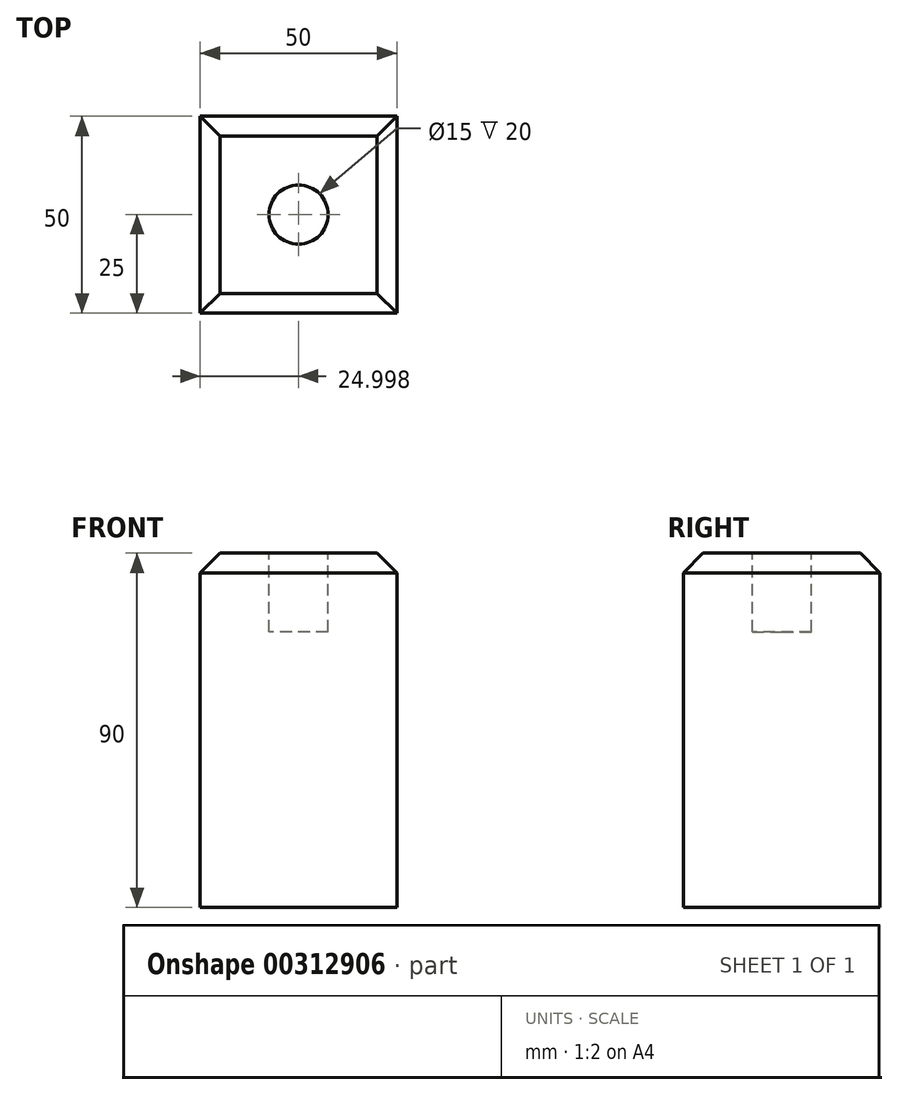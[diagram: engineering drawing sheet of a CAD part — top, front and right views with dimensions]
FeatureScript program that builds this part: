
annotation { "Feature Type Name" : "Feature", "Feature Type Description" : "" }
export const myFeature = defineFeature(function(context is Context, id is Id, definition is map)
    precondition{}
    {
        {
            var Q0;
            Q0=qCreatedBy(makeId("Top.planeOp"),FACE);
            var sketch = newSketch(context, id + "F0", { "sketchPlane" : qUnion([Q0])});
            skLineSegment(sketch, "E0", {"start": v(-33.76, -27.68) * mm, "end": v(-33.76, 22.32) * mm});
            skLineSegment(sketch, "E1", {"start": v(-33.76, 22.32) * mm, "end": v(16.24, 22.32) * mm});
            skLineSegment(sketch, "E2", {"start": v(16.24, 22.32) * mm, "end": v(16.24, -27.68) * mm});
            skLineSegment(sketch, "E3", {"start": v(16.24, -27.68) * mm, "end": v(-33.76, -27.68) * mm});
            skSolve(sketch);
        }
        {
            var Q0;
            Q0=makeQuery(id+"F0.imprint","IMPRINT",FACE,{"disambiguationData":[TD([[makeQuery(id+"F0.imprint","IMPRINT",EDGE,{"derivedFrom":sQuery(id+"F0.wireOp",EDGE,"E0")}),-1.0]])]});
            extrude(context, id + "F1", {"entities" : qUnion([Q0]), "depth" : 90 * mm});
        }
        {
            var Q0;
            Q0=makeQuery(id+"F1.opExtrude","CAP_FACE",FACE,{"disambiguationData":[OSD([sQuery(id+"F0.wireOp",EDGE,"E0"),sQuery(id+"F0.wireOp",EDGE,"E1"),sQuery(id+"F0.wireOp",EDGE,"E2"),sQuery(id+"F0.wireOp",EDGE,"E3")])],"isStart":false});
            chamfer(context, id + "F2", {"entities" : qUnion([Q0]), "width" : 5 * mm, "tangentPropagation" : true});
        }
        {
            var Q0;
            Q0=makeQuery(id+"F1.opExtrude","CAP_FACE",FACE,{"disambiguationData":[OSD([sQuery(id+"F0.wireOp",EDGE,"E0"),sQuery(id+"F0.wireOp",EDGE,"E1"),sQuery(id+"F0.wireOp",EDGE,"E2"),sQuery(id+"F0.wireOp",EDGE,"E3")])],"isStart":false});
            var sketch = newSketch(context, id + "F3", { "sketchPlane" : qUnion([Q0])});
            skSolve(sketch);
        }
        {
            var Q0;
            {var subQ0=sQuery(id+"F0.wireOp",EDGE,"E3");var subQ1=sQuery(id+"F0.wireOp",EDGE,"E2");var subQ2=sQuery(id+"F0.wireOp",EDGE,"E1");var subQ3=sQuery(id+"F0.wireOp",EDGE,"E0");var subQ4=makeQuery(id+"F1.opExtrude","CAP_FACE",FACE,{"disambiguationData":[OSD([subQ3,subQ2,subQ1,subQ0])],"isStart":false});Q0=makeQuery(id+"F3.imprint","IMPRINT",FACE,{"disambiguationData":[TD([[makeQuery(id+"F3.imprint","IMPRINT",EDGE,{"derivedFrom":makeQuery(id+"F2.opChamfer","BLEND_EDGE",EDGE,{"blendedFrom":[makeQuery(id+"F1.opExtrude","CAP_EDGE",EDGE,{"disambiguationData":[OSD([subQ3])],"isStart":false}),subQ4],"blendedInto":[subQ4]})}),1.0]])]});}
            var sketch = newSketch(context, id + "F4", { "sketchPlane" : qUnion([Q0])});
            skCircle(sketch, "E4", {"center": v(-8.76, -2.68) * mm, "radius": 7.5 * mm});
            skSolve(sketch);
        }
        {
            var Q0;
            Q0=makeQuery(id+"F4.imprint","IMPRINT",FACE,{"disambiguationData":[TD([[makeQuery(id+"F4.imprint","IMPRINT",EDGE,{"derivedFrom":sQuery(id+"F4.wireOp",EDGE,"E4")}),1.0]])]});
            extrude(context, id + "F5", {"entities" : qUnion([Q0]), "operationType" : NewBodyOperationType.REMOVE, "oppositeDirection" : true, "depth" : 20 * mm});
        }
    });
